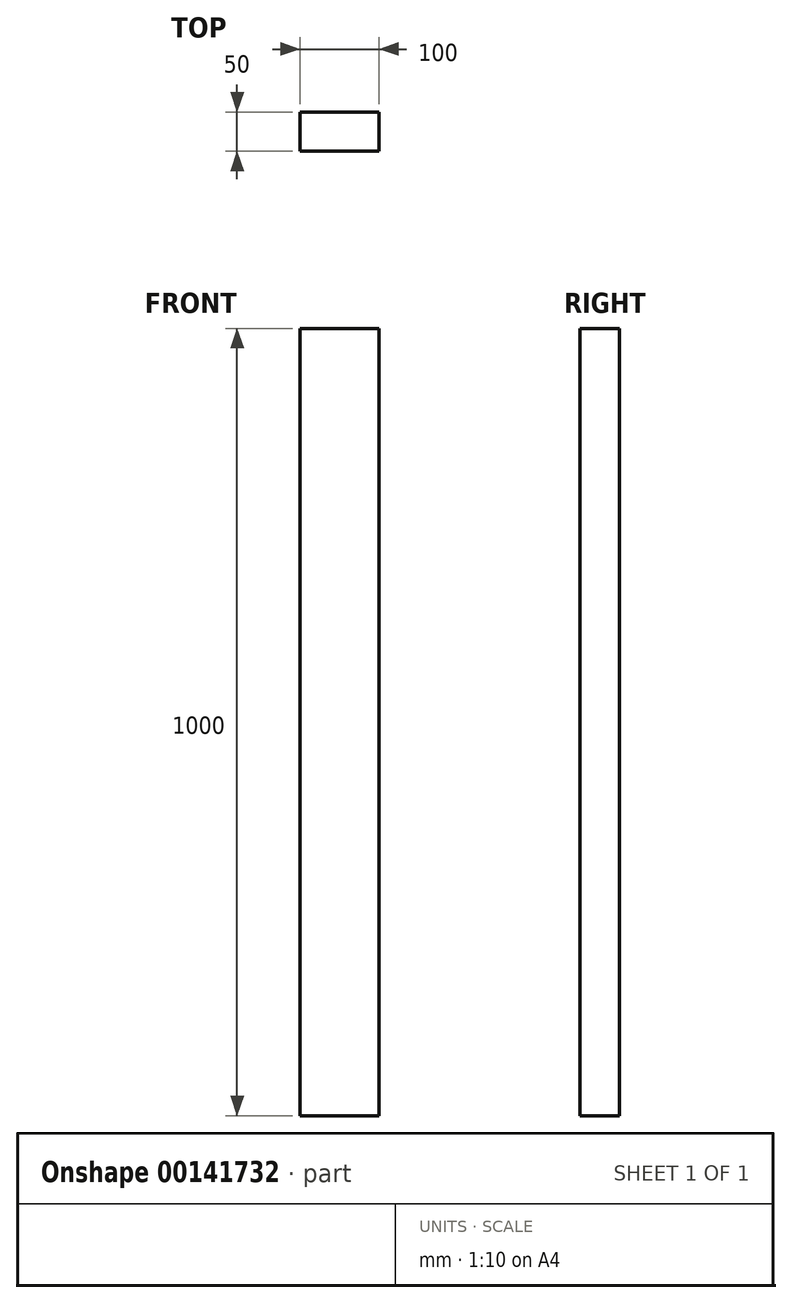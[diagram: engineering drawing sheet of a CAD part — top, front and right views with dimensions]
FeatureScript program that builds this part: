
annotation { "Feature Type Name" : "Feature", "Feature Type Description" : "" }
export const myFeature = defineFeature(function(context is Context, id is Id, definition is map)
    precondition{}
    {
        {
            var Q0;
            Q0=qCreatedBy(makeId("Top.planeOp"),FACE);
            var sketch = newSketch(context, id + "F0", { "sketchPlane" : qUnion([Q0])});
            skLineSegment(sketch, "E0.bottom", {"start": v(50, 25) * mm, "end": v(-50, 25) * mm});
            skLineSegment(sketch, "E0.top", {"start": v(50, -25) * mm, "end": v(-50, -25) * mm});
            skLineSegment(sketch, "E0.left", {"start": v(50, 25) * mm, "end": v(50, -25) * mm});
            skLineSegment(sketch, "E0.right", {"start": v(-50, 25) * mm, "end": v(-50, -25) * mm});
            skPoint(sketch, "E0.middle", {"position": v(0, 0) * mm});
            skSolve(sketch);
        }
        {
            var Q0;
            Q0 = qSketchRegion(id + "F0", true);
            extrude(context, id + "F1", {"entities" : qUnion([Q0]), "depth" : 1000 * mm});
        }
    });
